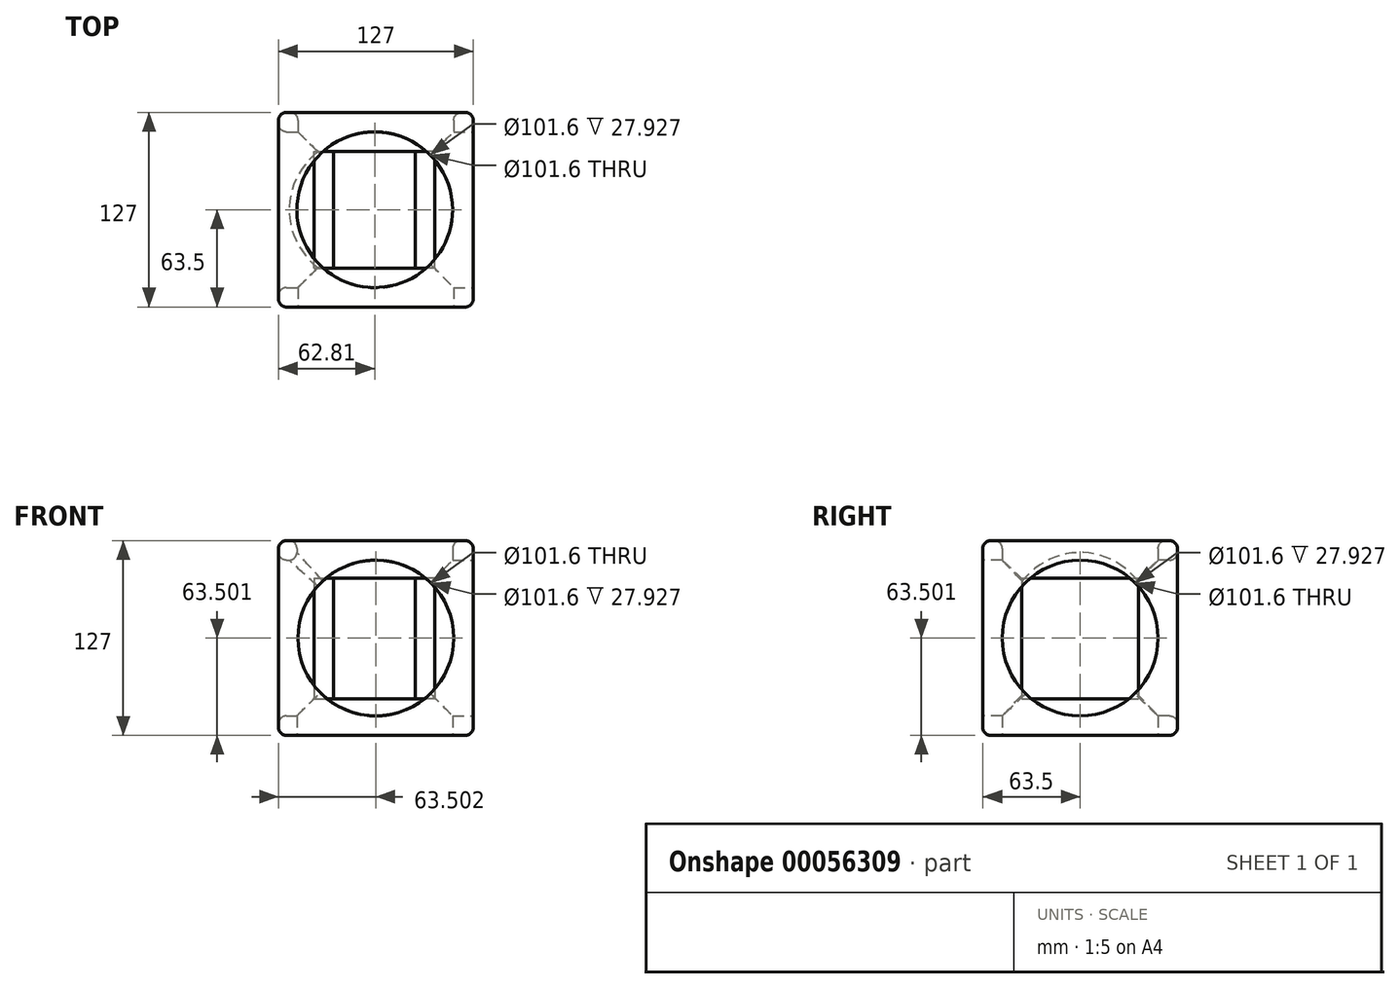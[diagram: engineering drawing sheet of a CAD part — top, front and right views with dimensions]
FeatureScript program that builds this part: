
annotation { "Feature Type Name" : "Feature", "Feature Type Description" : "" }
export const myFeature = defineFeature(function(context is Context, id is Id, definition is map)
    precondition{}
    {
        {
            var Q0;
            Q0=qCreatedBy(makeId("Front.planeOp"),FACE);
            var sketch = newSketch(context, id + "F0", { "sketchPlane" : qUnion([Q0])});
            skLineSegment(sketch, "E0.bottom", {"start": v(-62.8, 68.5) * mm, "end": v(64.2, 68.5) * mm});
            skLineSegment(sketch, "E0.top", {"start": v(-62.8, -58.5) * mm, "end": v(64.2, -58.5) * mm});
            skLineSegment(sketch, "E0.left", {"start": v(-62.8, 68.5) * mm, "end": v(-62.8, -58.5) * mm});
            skLineSegment(sketch, "E0.right", {"start": v(64.2, 68.5) * mm, "end": v(64.2, -58.5) * mm});
            skSolve(sketch);
        }
        {
            var Q0;
            Q0 = qSketchRegion(id + "F0", true);
            extrude(context, id + "F1", {"entities" : qUnion([Q0]), "depth" : 127 * mm});
        }
        {
            var Q0;
            Q0=makeQuery(id+"F1.opExtrude","CAP_FACE",FACE,{"disambiguationData":[OSD([sQuery(id+"F0.wireOp",EDGE,"E0.bottom"),sQuery(id+"F0.wireOp",EDGE,"E0.top"),sQuery(id+"F0.wireOp",EDGE,"E0.left"),sQuery(id+"F0.wireOp",EDGE,"E0.right")])],"isStart":false});
            var sketch = newSketch(context, id + "F2", { "sketchPlane" : qUnion([Q0])});
            skLineSegment(sketch, "E1", {"start": v(-62.8, -58.5) * mm, "end": v(64.2, 68.5) * mm, "construction": true});
            skCircle(sketch, "E2", {"center": v(0.7, 5) * mm, "radius": 50.8 * mm});
            skSolve(sketch);
        }
        {
            var Q0;
            Q0 = qSketchRegion(id + "F2", true);
            extrude(context, id + "F3", {"entities" : qUnion([Q0]), "operationType" : NewBodyOperationType.REMOVE, "endBound" : BoundingType.THROUGH_ALL, "oppositeDirection" : true, "depth" : 25.4 * mm});
        }
        {
            var Q0;
            Q0=makeQuery(id+"F1.opExtrude","SWEPT_FACE",FACE,{"disambiguationData":[OSD([sQuery(id+"F0.wireOp",EDGE,"E0.top")])]});
            var sketch = newSketch(context, id + "F4", { "sketchPlane" : qUnion([Q0])});
            skLineSegment(sketch, "E3", {"start": v(-62.8, 0) * mm, "end": v(64.2, 127) * mm, "construction": true});
            skCircle(sketch, "E4", {"center": v(0, 63.5) * mm, "radius": 50.8 * mm});
            skPoint(sketch, "E4.centerSnap0", {"position": v(0.7, 63.5) * mm});
            skSolve(sketch);
        }
        {
            var Q0;
            Q0=makeQuery(id+"F4.imprint","IMPRINT",FACE,{"disambiguationData":[TD([[makeQuery(id+"F4.imprint","IMPRINT",EDGE,{"derivedFrom":sQuery(id+"F4.wireOp",EDGE,"E4")}),1.0]])]});
            extrude(context, id + "F5", {"entities" : qUnion([Q0]), "operationType" : NewBodyOperationType.REMOVE, "endBound" : BoundingType.THROUGH_ALL, "oppositeDirection" : true, "depth" : 25.4 * mm});
        }
        {
            var Q0;
            Q0=makeQuery(id+"F1.opExtrude","SWEPT_FACE",FACE,{"disambiguationData":[OSD([sQuery(id+"F0.wireOp",EDGE,"E0.right")])]});
            var sketch = newSketch(context, id + "F6", { "sketchPlane" : qUnion([Q0])});
            skLineSegment(sketch, "E5", {"start": v(-127, 68.5) * mm, "end": v(0, -58.5) * mm, "construction": true});
            skCircle(sketch, "E6", {"center": v(-63.5, 5) * mm, "radius": 50.8 * mm});
            skSolve(sketch);
        }
        {
            var Q0;
            Q0 = qSketchRegion(id + "F6", true);
            extrude(context, id + "F7", {"entities" : qUnion([Q0]), "operationType" : NewBodyOperationType.REMOVE, "endBound" : BoundingType.THROUGH_ALL, "oppositeDirection" : true, "depth" : 25.4 * mm});
        }
        {
            var Q0;
            Q0=qCreatedBy(makeId("Front.planeOp"),FACE);
            var sketch = newSketch(context, id + "F8", { "sketchPlane" : qUnion([Q0])});
            skLineSegment(sketch, "E7.bottom", {"start": v(-26.87, 31.45) * mm, "end": v(26.47, 31.45) * mm});
            skLineSegment(sketch, "E7.top", {"start": v(-26.87, -21.89) * mm, "end": v(26.47, -21.89) * mm});
            skLineSegment(sketch, "E7.left", {"start": v(-26.87, 31.45) * mm, "end": v(-26.87, -21.89) * mm});
            skLineSegment(sketch, "E7.right", {"start": v(26.47, 31.45) * mm, "end": v(26.47, -21.89) * mm});
            skSolve(sketch);
        }
        {
            var Q0;
            Q0 = qSketchRegion(id + "F8", true);
            extrude(context, id + "F9", {"entities" : qUnion([Q0]), "depth" : 101.6 * mm});
        }
        {
            var Q0;
            Q0=makeQuery(id+"F9.opExtrude","CAP_FACE",FACE,{"disambiguationData":[OSD([sQuery(id+"F8.wireOp",EDGE,"E7.bottom"),sQuery(id+"F8.wireOp",EDGE,"E7.top"),sQuery(id+"F8.wireOp",EDGE,"E7.left"),sQuery(id+"F8.wireOp",EDGE,"E7.right")])],"isStart":true});
            extrude(context, id + "F10", {"entities" : qUnion([Q0]), "operationType" : NewBodyOperationType.REMOVE, "oppositeDirection" : true, "depth" : 25.4 * mm});
        }
        {
            var Q0;
            Q0=makeQuery(id+"F9.opExtrude","SWEPT_FACE",FACE,{"disambiguationData":[OSD([sQuery(id+"F8.wireOp",EDGE,"E7.bottom")])]});
            extrude(context, id + "F11", {"entities" : qUnion([Q0]), "operationType" : NewBodyOperationType.ADD, "depth" : 12.7 * mm});
        }
        {
            var Q0;
            Q0=makeQuery(id+"F9.opExtrude","SWEPT_FACE",FACE,{"disambiguationData":[OSD([sQuery(id+"F8.wireOp",EDGE,"E7.top")])]});
            extrude(context, id + "F12", {"entities" : qUnion([Q0]), "operationType" : NewBodyOperationType.ADD, "depth" : 12.7 * mm});
        }
        {
            var Q0;
            {var subQ0=sQuery(id+"F8.wireOp",EDGE,"E7.right");Q0=makeQuery(id+"F12.boolean.opBoolean","MERGE",FACE,{"derivedFrom":[makeQuery(id+"F11.boolean.opBoolean","MERGE",FACE,{"derivedFrom":[makeQuery(id+"F9.opExtrude","SWEPT_FACE",FACE,{"disambiguationData":[OSD([subQ0])]}),makeQuery(id+"F11.opExtrude","SWEPT_FACE",FACE,{"disambiguationData":[OSD([sQuery(id+"F8.wireOp",EDGE,"E7.bottom"),subQ0])]})]}),makeQuery(id+"F12.opExtrude","SWEPT_FACE",FACE,{"disambiguationData":[OSD([sQuery(id+"F8.wireOp",EDGE,"E7.top"),subQ0])]})]});}
            extrude(context, id + "F13", {"entities" : qUnion([Q0]), "depth" : 12.7 * mm});
        }
        {
            var Q0;
            {var subQ0=sQuery(id+"F8.wireOp",EDGE,"E7.left");Q0=makeQuery(id+"F12.boolean.opBoolean","MERGE",FACE,{"derivedFrom":[makeQuery(id+"F11.boolean.opBoolean","MERGE",FACE,{"derivedFrom":[makeQuery(id+"F9.opExtrude","SWEPT_FACE",FACE,{"disambiguationData":[OSD([subQ0])]}),makeQuery(id+"F11.opExtrude","SWEPT_FACE",FACE,{"disambiguationData":[OSD([sQuery(id+"F8.wireOp",EDGE,"E7.bottom"),subQ0])]})]}),makeQuery(id+"F12.opExtrude","SWEPT_FACE",FACE,{"disambiguationData":[OSD([sQuery(id+"F8.wireOp",EDGE,"E7.top"),subQ0])]})]});}
            extrude(context, id + "F14", {"entities" : qUnion([Q0]), "depth" : 12.7 * mm});
        }
        {
            var Q0;
            Q0=makeQuery(id+"F1.opExtrude","CAP_EDGE",EDGE,{"disambiguationData":[OSD([sQuery(id+"F0.wireOp",EDGE,"E0.bottom")])],"isStart":false});
            var Q1;
            Q1=makeQuery(id+"F1.opExtrude","CAP_EDGE",EDGE,{"disambiguationData":[OSD([sQuery(id+"F0.wireOp",EDGE,"E0.right")])],"isStart":false});
            var Q2;
            Q2=makeQuery(id+"F1.opExtrude","SWEPT_EDGE",EDGE,{"disambiguationData":[OSD([sQuery(id+"F0.wireOp",EDGE,"E0.bottom"),sQuery(id+"F0.wireOp",EDGE,"E0.right")])]});
            var Q3;
            Q3=makeQuery(id+"F1.opExtrude","SWEPT_EDGE",EDGE,{"disambiguationData":[OSD([sQuery(id+"F0.wireOp",EDGE,"E0.top"),sQuery(id+"F0.wireOp",EDGE,"E0.right")])]});
            var Q4;
            Q4=makeQuery(id+"F1.opExtrude","CAP_EDGE",EDGE,{"disambiguationData":[OSD([sQuery(id+"F0.wireOp",EDGE,"E0.right")])],"isStart":true});
            var Q5;
            Q5=makeQuery(id+"F1.opExtrude","CAP_EDGE",EDGE,{"disambiguationData":[OSD([sQuery(id+"F0.wireOp",EDGE,"E0.left")])],"isStart":false});
            var Q6;
            Q6=makeQuery(id+"F1.opExtrude","CAP_EDGE",EDGE,{"disambiguationData":[OSD([sQuery(id+"F0.wireOp",EDGE,"E0.top")])],"isStart":false});
            var Q7;
            Q7=makeQuery(id+"F1.opExtrude","SWEPT_EDGE",EDGE,{"disambiguationData":[OSD([sQuery(id+"F0.wireOp",EDGE,"E0.bottom"),sQuery(id+"F0.wireOp",EDGE,"E0.left")])]});
            var Q8;
            Q8=makeQuery(id+"F1.opExtrude","CAP_EDGE",EDGE,{"disambiguationData":[OSD([sQuery(id+"F0.wireOp",EDGE,"E0.bottom")])],"isStart":true});
            var Q9;
            Q9=makeQuery(id+"F3.boolean.opBoolean","COPY",EDGE,{"derivedFrom":makeQuery(id+"F3.opExtrude","CAP_EDGE",EDGE,{"disambiguationData":[OSD([sQuery(id+"F2.wireOp",EDGE,"E2")])],"isStart":true})});
            var Q10;
            Q10=makeQuery(id+"F5.boolean.opBoolean","INTERSECT",EDGE,{"derivedFrom":[makeQuery(id+"F1.opExtrude","SWEPT_FACE",FACE,{"disambiguationData":[OSD([sQuery(id+"F0.wireOp",EDGE,"E0.bottom")])]}),makeQuery(id+"F5.opExtrude","SWEPT_FACE",FACE,{"disambiguationData":[OSD([sQuery(id+"F4.wireOp",EDGE,"E4")])]})]});
            var Q11;
            Q11=makeQuery(id+"F1.opExtrude","CAP_EDGE",EDGE,{"disambiguationData":[OSD([sQuery(id+"F0.wireOp",EDGE,"E0.left")])],"isStart":true});
            var Q12;
            Q12=makeQuery(id+"F1.opExtrude","SWEPT_FACE",FACE,{"disambiguationData":[OSD([sQuery(id+"F0.wireOp",EDGE,"E0.left")])]});
            var Q13;
            Q13=makeQuery(id+"F1.opExtrude","SWEPT_EDGE",EDGE,{"disambiguationData":[OSD([sQuery(id+"F0.wireOp",EDGE,"E0.top"),sQuery(id+"F0.wireOp",EDGE,"E0.left")])]});
            var Q14;
            Q14=makeQuery(id+"F5.boolean.opBoolean","COPY",EDGE,{"derivedFrom":makeQuery(id+"F5.opExtrude","CAP_EDGE",EDGE,{"disambiguationData":[OSD([sQuery(id+"F4.wireOp",EDGE,"E4")])],"isStart":true})});
            var Q15;
            Q15=makeQuery(id+"F1.opExtrude","CAP_EDGE",EDGE,{"disambiguationData":[OSD([sQuery(id+"F0.wireOp",EDGE,"E0.top")])],"isStart":true});
            var Q16;
            Q16=makeQuery(id+"F7.boolean.opBoolean","INTERSECT",EDGE,{"disambiguationData":[OD(0.0)],"derivedFrom":[makeQuery(id+"F5.boolean.opBoolean","COPY",FACE,{"derivedFrom":makeQuery(id+"F5.opExtrude","SWEPT_FACE",FACE,{"disambiguationData":[OSD([sQuery(id+"F4.wireOp",EDGE,"E4")])]})}),makeQuery(id+"F7.opExtrude","SWEPT_FACE",FACE,{"disambiguationData":[OSD([sQuery(id+"F6.wireOp",EDGE,"E6")])]})]});
            var Q17;
            Q17=makeQuery(id+"F7.boolean.opBoolean","COPY",EDGE,{"derivedFrom":makeQuery(id+"F7.opExtrude","CAP_EDGE",EDGE,{"disambiguationData":[OSD([sQuery(id+"F6.wireOp",EDGE,"E6")])],"isStart":true})});
            var Q18;
            Q18=makeQuery(id+"F3.boolean.opBoolean","INTERSECT",EDGE,{"derivedFrom":[makeQuery(id+"F1.opExtrude","CAP_FACE",FACE,{"disambiguationData":[OSD([sQuery(id+"F0.wireOp",EDGE,"E0.bottom"),sQuery(id+"F0.wireOp",EDGE,"E0.top"),sQuery(id+"F0.wireOp",EDGE,"E0.left"),sQuery(id+"F0.wireOp",EDGE,"E0.right")])],"isStart":true}),makeQuery(id+"F3.opExtrude","SWEPT_FACE",FACE,{"disambiguationData":[OSD([sQuery(id+"F2.wireOp",EDGE,"E2")])]})]});
            fillet(context, id + "F15", {"entities" : qUnion([Q0, Q1, Q2, Q3, Q4, Q5, Q6, Q7, Q8, Q9, Q10, Q11, Q12, Q13, Q14, Q15, Q16, Q17, Q18]), "radius" : 5.08 * mm, "tangentPropagation" : true, "allowEdgeOverflow" : false});
        }
    });
